# Revit family: O74111001_Lavamanos Manantial Duo para Sobreponer Blanco
name_source: partatom
category: Plumbing Fixtures
units: mm (PartAtom-declared; Revit-internal decimal feet)

## family parameters
Cut with Voids When Loaded = No
Host = Face
OmniClass Number = 23.31.13.11
OmniClass Title = Single Sinks
Part Type = Normal
Room Calculation Point = No
Round Connector Dimension = Use Radius
Shared = No

## types (1)
- O74111001_Lavamanos Manantial Duo para Sobreponer Blanco
    Acabado = Brillante
    Alto = 15.2 cm
    Ancho = 39.5 cm
    Colección = Lavamanos 2008
    Creado por = IDD
    Default Elevation = 122 cm
    Description = Un lavamanos que cuenta con diseño con doble propósito para instalar sobrepuesto en el mesón o tipo vessel. Tiene un práctico tamaño para espacios reducidos y se recomienda instalar con griferías a la pared o de mesón.
    Dimensión del pozo = 34.5
    Diámetro del desagüe = 101.6 mm
    Fecha de creación = 30/07/2020
    Forma = Redondo
    Garantía = Garantía completa para siempre en la porcelana
    Largo = 39.5 cm
    Línea = Manantial
    Material = Corona_Porcelana_Sanitaria
    Materiales = Porcelana sanitaria
    No incluye = Grifería
    Productos compatibles = Grifería monocontrol media
    Profundidad del pozo = 13.5 cm
    Resistencia = Alta resistencia al rayado y cambios de temperatura
    Tecnologías = CoverGloss Aquaflow
    Tipo de desagüe = Expuesto
    Tipo de instalación = A pared
    Tipo de lavamanos = Para sobreponer
    URL = https://corona.co
    Uso = Residencial

## geometry (parser evidence)
native form markers: Sweep x9
no freeform markers — native parametric forms only
